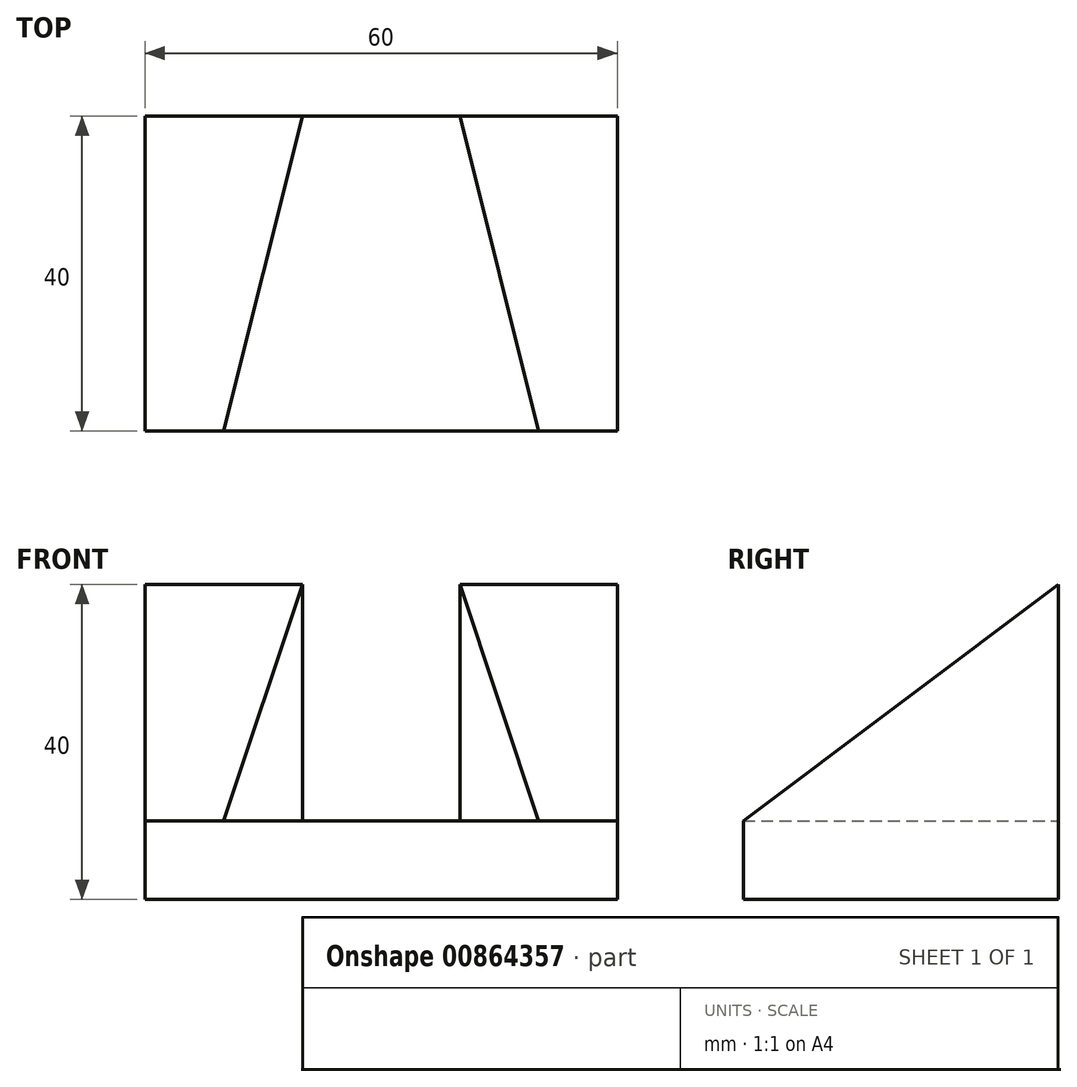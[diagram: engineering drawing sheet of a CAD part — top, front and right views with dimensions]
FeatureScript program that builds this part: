
annotation { "Feature Type Name" : "Feature", "Feature Type Description" : "" }
export const myFeature = defineFeature(function(context is Context, id is Id, definition is map)
    precondition{}
    {
        {
            var Q0;
            Q0=qCreatedBy(makeId("Top.planeOp"),FACE);
            var sketch = newSketch(context, id + "F0", { "sketchPlane" : qUnion([Q0])});
            skLineSegment(sketch, "E0.bottom", {"start": v(0, 0) * mm, "end": v(60, 0) * mm});
            skLineSegment(sketch, "E0.top", {"start": v(0, 40) * mm, "end": v(60, 40) * mm});
            skLineSegment(sketch, "E0.left", {"start": v(0, 0) * mm, "end": v(0, 40) * mm});
            skLineSegment(sketch, "E0.right", {"start": v(60, 0) * mm, "end": v(60, 40) * mm});
            skLineSegment(sketch, "E1", {"start": v(10, 0) * mm, "end": v(20, 40) * mm});
            skLineSegment(sketch, "E2", {"start": v(50, 0) * mm, "end": v(40, 40) * mm});
            skLineSegment(sketch, "E3", {"start": v(30, 40) * mm, "end": v(30, 0) * mm, "construction": true});
            skSolve(sketch);
        }
        {
            var Q0;
            {var subQ0=sQuery(id+"F0.wireOp",EDGE,"E0.left");Q0=makeQuery(id+"F0.imprint","IMPRINT",FACE,{"disambiguationData":[TD([[makeQuery(id+"F0.imprint","IMPRINT",EDGE,{"derivedFrom":subQ0}),-1.0]])]});}
            var Q1;
            {var subQ0=sQuery(id+"F0.wireOp",EDGE,"E1");Q1=makeQuery(id+"F0.imprint","IMPRINT",FACE,{"disambiguationData":[TD([[makeQuery(id+"F0.imprint","IMPRINT",EDGE,{"derivedFrom":subQ0}),-1.0]])]});}
            var Q2;
            {var subQ0=sQuery(id+"F0.wireOp",EDGE,"E0.right");Q2=makeQuery(id+"F0.imprint","IMPRINT",FACE,{"disambiguationData":[TD([[makeQuery(id+"F0.imprint","IMPRINT",EDGE,{"derivedFrom":subQ0}),1.0]])]});}
            extrude(context, id + "F1", {"entities" : qUnion([Q0, Q1, Q2]), "oppositeDirection" : true, "depth" : 10 * mm, "offsetDistance" : 25 * mm});
        }
        {
            var Q0;
            {var subQ0=sQuery(id+"F0.wireOp",EDGE,"E0.left");Q0=makeQuery(id+"F0.imprint","IMPRINT",FACE,{"disambiguationData":[TD([[makeQuery(id+"F0.imprint","IMPRINT",EDGE,{"derivedFrom":subQ0}),-1.0]])]});}
            var Q1;
            {var subQ0=sQuery(id+"F0.wireOp",EDGE,"E0.right");Q1=makeQuery(id+"F0.imprint","IMPRINT",FACE,{"disambiguationData":[TD([[makeQuery(id+"F0.imprint","IMPRINT",EDGE,{"derivedFrom":subQ0}),1.0]])]});}
            extrude(context, id + "F2", {"entities" : qUnion([Q0, Q1]), "operationType" : NewBodyOperationType.ADD, "depth" : 30 * mm, "offsetDistance" : 25 * mm});
        }
        {
            var Q0;
            {var subQ0=sQuery(id+"F0.wireOp",EDGE,"E0.bottom");Q0=makeQuery(id+"F2.opExtrude","CAP_EDGE",EDGE,{"disambiguationData":[OSD([subQ0]),TDD([makeQuery(id+"F0.imprint","IMPRINT",EDGE,{"disambiguationData":[TD([[makeQuery(id+"F0.imprint","INTERSECT",VERTEX,{"derivedFrom":[subQ0,sQuery(id+"F0.wireOp",EDGE,"E0.left")]}),-1.0]])],"derivedFrom":subQ0})])],"isStart":false});}
            var Q1;
            {var subQ0=sQuery(id+"F0.wireOp",EDGE,"E0.bottom");Q1=makeQuery(id+"F2.opExtrude","CAP_EDGE",EDGE,{"disambiguationData":[OSD([subQ0]),TDD([makeQuery(id+"F0.imprint","IMPRINT",EDGE,{"disambiguationData":[TD([[makeQuery(id+"F0.imprint","INTERSECT",VERTEX,{"derivedFrom":[subQ0,sQuery(id+"F0.wireOp",EDGE,"E0.right")]}),1.0]])],"derivedFrom":subQ0})])],"isStart":false});}
            chamfer(context, id + "F3", {"entities" : qUnion([Q0, Q1]), "chamferType" : ChamferType.TWO_OFFSETS, "width1" : 40 * mm, "oppositeDirection" : false, "width2" : 30 * mm, "tangentPropagation" : true});
        }
    });
